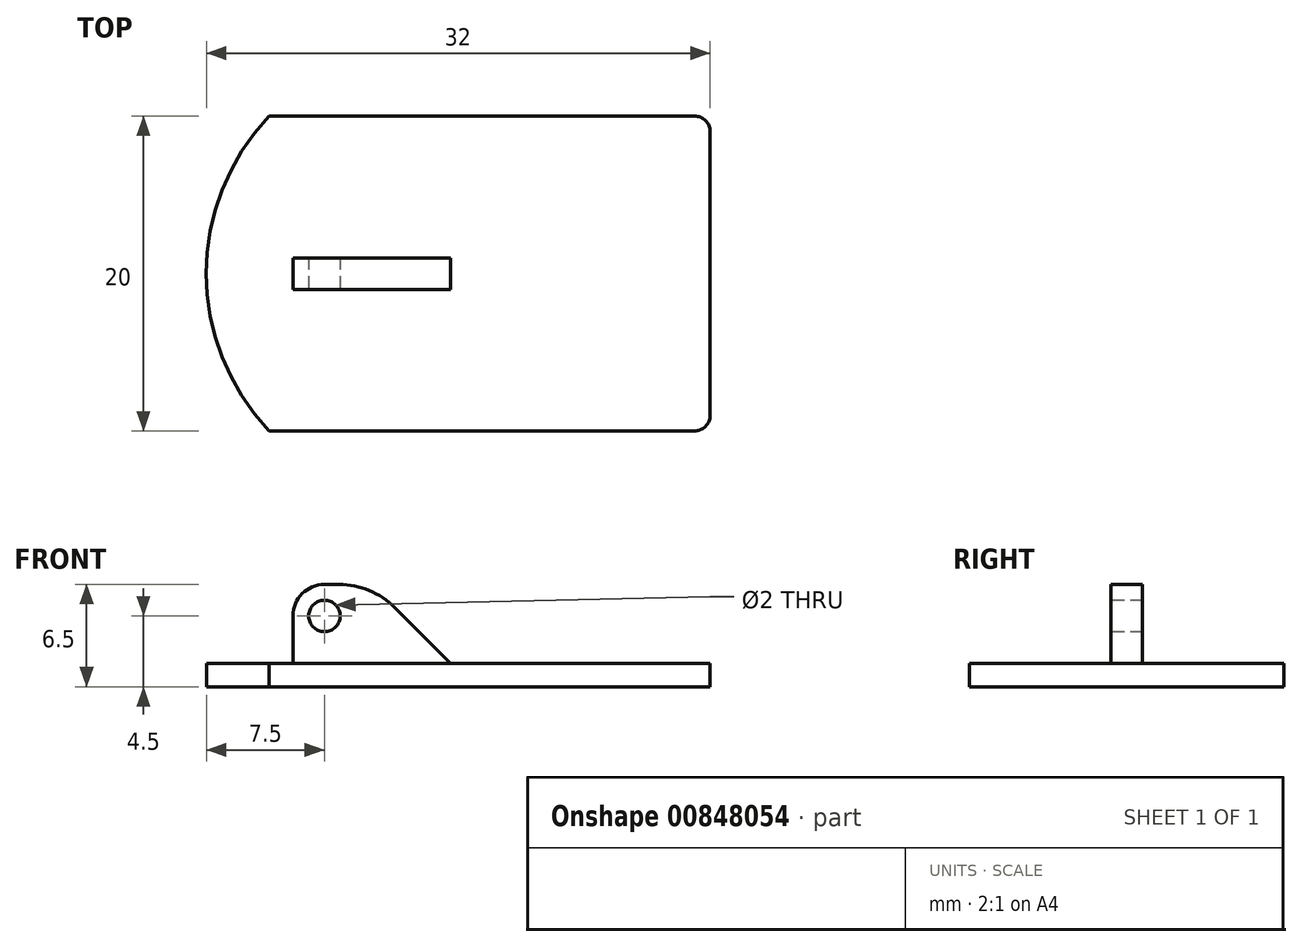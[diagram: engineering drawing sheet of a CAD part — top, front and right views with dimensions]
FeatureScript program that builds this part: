
annotation { "Feature Type Name" : "Feature", "Feature Type Description" : "" }
export const myFeature = defineFeature(function(context is Context, id is Id, definition is map)
    precondition{}
    {
        {
            var Q0;
            Q0=qCreatedBy(makeId("Top.planeOp"),FACE);
            var sketch = newSketch(context, id + "F0", { "sketchPlane" : qUnion([Q0])});
            skLineSegment(sketch, "E0.bottom", {"start": v(14, 10) * mm, "end": v(-14, 10) * mm});
            skLineSegment(sketch, "E0.top", {"start": v(14, -10) * mm, "end": v(-14, -10) * mm});
            skLineSegment(sketch, "E0.left", {"start": v(14, 10) * mm, "end": v(14, -10) * mm});
            skLineSegment(sketch, "E0.right", {"start": v(-14, 10) * mm, "end": v(-14, -10) * mm});
            skPoint(sketch, "E0.middle", {"position": v(0, 0) * mm});
            skSolve(sketch);
        }
        {
            var Q0;
            Q0=makeQuery(id+"F0.imprint","IMPRINT",FACE,{"disambiguationData":[TD([[makeQuery(id+"F0.imprint","IMPRINT",EDGE,{"derivedFrom":sQuery(id+"F0.wireOp",EDGE,"E0.bottom")}),1.0]])]});
            extrude(context, id + "F1", {"entities" : qUnion([Q0]), "depth" : 1.5 * mm, "offsetDistance" : 25 * mm});
        }
        {
            var Q0;
            Q0=makeQuery(id+"F1.opExtrude","SWEPT_EDGE",EDGE,{"disambiguationData":[OSD([sQuery(id+"F0.wireOp",EDGE,"E0.top"),sQuery(id+"F0.wireOp",EDGE,"E0.left")])]});
            var Q1;
            Q1=makeQuery(id+"F1.opExtrude","SWEPT_EDGE",EDGE,{"disambiguationData":[OSD([sQuery(id+"F0.wireOp",EDGE,"E0.bottom"),sQuery(id+"F0.wireOp",EDGE,"E0.left")])]});
            fillet(context, id + "F2", {"entities" : qUnion([Q0, Q1]), "radius" : 1 * mm, "tangentPropagation" : true, "allowEdgeOverflow" : false});
        }
        {
            var Q0;
            Q0=makeQuery(id+"F1.opExtrude","CAP_FACE",FACE,{"disambiguationData":[OSD([sQuery(id+"F0.wireOp",EDGE,"E0.bottom"),sQuery(id+"F0.wireOp",EDGE,"E0.top"),sQuery(id+"F0.wireOp",EDGE,"E0.left"),sQuery(id+"F0.wireOp",EDGE,"E0.right")])],"isStart":false});
            var sketch = newSketch(context, id + "F3", { "sketchPlane" : qUnion([Q0])});
            skLineSegment(sketch, "E1.bottom", {"start": v(-12.5, 0) * mm, "end": v(-2.5, 0) * mm});
            skLineSegment(sketch, "E1.top", {"start": v(-12.5, 1) * mm, "end": v(-2.5, 1) * mm});
            skLineSegment(sketch, "E1.left", {"start": v(-12.5, 0) * mm, "end": v(-12.5, 1) * mm});
            skLineSegment(sketch, "E1.right", {"start": v(-2.5, 0) * mm, "end": v(-2.5, 1) * mm});
            skSolve(sketch);
        }
        {
            var Q0;
            Q0=makeQuery(id+"F3.imprint","IMPRINT",FACE,{"disambiguationData":[TD([[makeQuery(id+"F3.imprint","IMPRINT",EDGE,{"derivedFrom":sQuery(id+"F3.wireOp",EDGE,"E1.bottom")}),1.0]])]});
            extrude(context, id + "F4", {"entities" : qUnion([Q0]), "depth" : 5 * mm, "offsetDistance" : 25 * mm});
        }
        {
            var Q0;
            Q0=makeQuery(id+"F4.opExtrude","CAP_EDGE",EDGE,{"disambiguationData":[OSD([sQuery(id+"F3.wireOp",EDGE,"E1.left")])],"isStart":false});
            fillet(context, id + "F5", {"entities" : qUnion([Q0]), "radius" : 2 * mm, "tangentPropagation" : true, "allowEdgeOverflow" : false});
        }
        {
            var Q0;
            Q0=makeQuery(id+"F4.opExtrude","CAP_EDGE",EDGE,{"disambiguationData":[OSD([sQuery(id+"F3.wireOp",EDGE,"E1.right")])],"isStart":false});
            chamfer(context, id + "F6", {"entities" : qUnion([Q0]), "width" : 5 * mm, "tangentPropagation" : true});
        }
        {
            var Q0;
            {var subQ0=sQuery(id+"F3.wireOp",EDGE,"E1.right");Q0=makeQuery(id+"F6.opChamfer","BLEND_EDGE",EDGE,{"blendedFrom":[makeQuery(id+"F4.opExtrude","CAP_EDGE",EDGE,{"disambiguationData":[OSD([subQ0])],"isStart":false}),makeQuery(id+"F4.opExtrude","CAP_FACE",FACE,{"disambiguationData":[OSD([sQuery(id+"F3.wireOp",EDGE,"E1.bottom"),sQuery(id+"F3.wireOp",EDGE,"E1.top"),sQuery(id+"F3.wireOp",EDGE,"E1.left"),subQ0])],"isStart":false})],"blendedInto":[makeQuery(id+"F4.opExtrude","CAP_FACE",FACE,{"disambiguationData":[OSD([sQuery(id+"F3.wireOp",EDGE,"E1.bottom"),sQuery(id+"F3.wireOp",EDGE,"E1.top"),sQuery(id+"F3.wireOp",EDGE,"E1.left"),subQ0])],"isStart":false})]});}
            fillet(context, id + "F7", {"entities" : qUnion([Q0]), "radius" : 5 * mm, "tangentPropagation" : true, "allowEdgeOverflow" : false});
        }
        {
            var Q0;
            Q0=makeQuery(id+"F4.opExtrude","SWEPT_BODY",BODY,{"disambiguationData":[OSD([sQuery(id+"F3.wireOp",EDGE,"E1.bottom"),sQuery(id+"F3.wireOp",EDGE,"E1.top"),sQuery(id+"F3.wireOp",EDGE,"E1.left"),sQuery(id+"F3.wireOp",EDGE,"E1.right")])]});
            var Q1;
            Q1=qCreatedBy(makeId("Front.planeOp"),FACE);
            mirror(context, id + "F8", {"operationType" : NewBodyOperationType.ADD, "entities" : qUnion([Q0]), "mirrorPlane" : qUnion([Q1])});
        }
        {
            var Q0;
            Q0=makeQuery(id+"F8.opPattern","COPY",FACE,{"derivedFrom":makeQuery(id+"F4.opExtrude","SWEPT_FACE",FACE,{"disambiguationData":[OSD([sQuery(id+"F3.wireOp",EDGE,"E1.top")])]}),"instanceName":"1"});
            var sketch = newSketch(context, id + "F9", { "sketchPlane" : qUnion([Q0])});
            skCircle(sketch, "E2", {"center": v(-10.5, 4.5) * mm, "radius": 1 * mm});
            skSolve(sketch);
        }
        {
            var Q0;
            Q0=makeQuery(id+"F9.imprint","IMPRINT",FACE,{"disambiguationData":[TD([[makeQuery(id+"F9.imprint","IMPRINT",EDGE,{"derivedFrom":sQuery(id+"F9.wireOp",EDGE,"E2")}),1.0]])]});
            extrude(context, id + "F10", {"entities" : qUnion([Q0]), "operationType" : NewBodyOperationType.REMOVE, "oppositeDirection" : true, "depth" : 25 * mm, "offsetDistance" : 25 * mm});
        }
        {
            var Q0;
            Q0=makeQuery(id+"F1.opExtrude","CAP_FACE",FACE,{"disambiguationData":[OSD([sQuery(id+"F0.wireOp",EDGE,"E0.bottom"),sQuery(id+"F0.wireOp",EDGE,"E0.top"),sQuery(id+"F0.wireOp",EDGE,"E0.left"),sQuery(id+"F0.wireOp",EDGE,"E0.right")])],"isStart":true});
            var sketch = newSketch(context, id + "F11", { "sketchPlane" : qUnion([Q0])});
            skArc(sketch, "E3", {"start": v(-14, 10) * mm, "mid": v(-18, 0) * mm, "end": v(-14, -10) * mm});
            skPoint(sketch, "E3.first.point", {"position": v(-14, -10) * mm});
            skPoint(sketch, "E3.second.point", {"position": v(-18, 0) * mm});
            skPoint(sketch, "E3.third.point", {"position": v(-14, 10) * mm});
            skSolve(sketch);
        }
        {
            var Q0;
            Q0=makeQuery(id+"F11.imprint","IMPRINT",FACE,{"disambiguationData":[TD([[makeQuery(id+"F11.imprint","IMPRINT",EDGE,{"derivedFrom":sQuery(id+"F11.wireOp",EDGE,"E3")}),1.0]])]});
            extrude(context, id + "F12", {"entities" : qUnion([Q0]), "operationType" : NewBodyOperationType.ADD, "oppositeDirection" : true, "depth" : 1.5 * mm, "offsetDistance" : 25 * mm});
        }
    });
